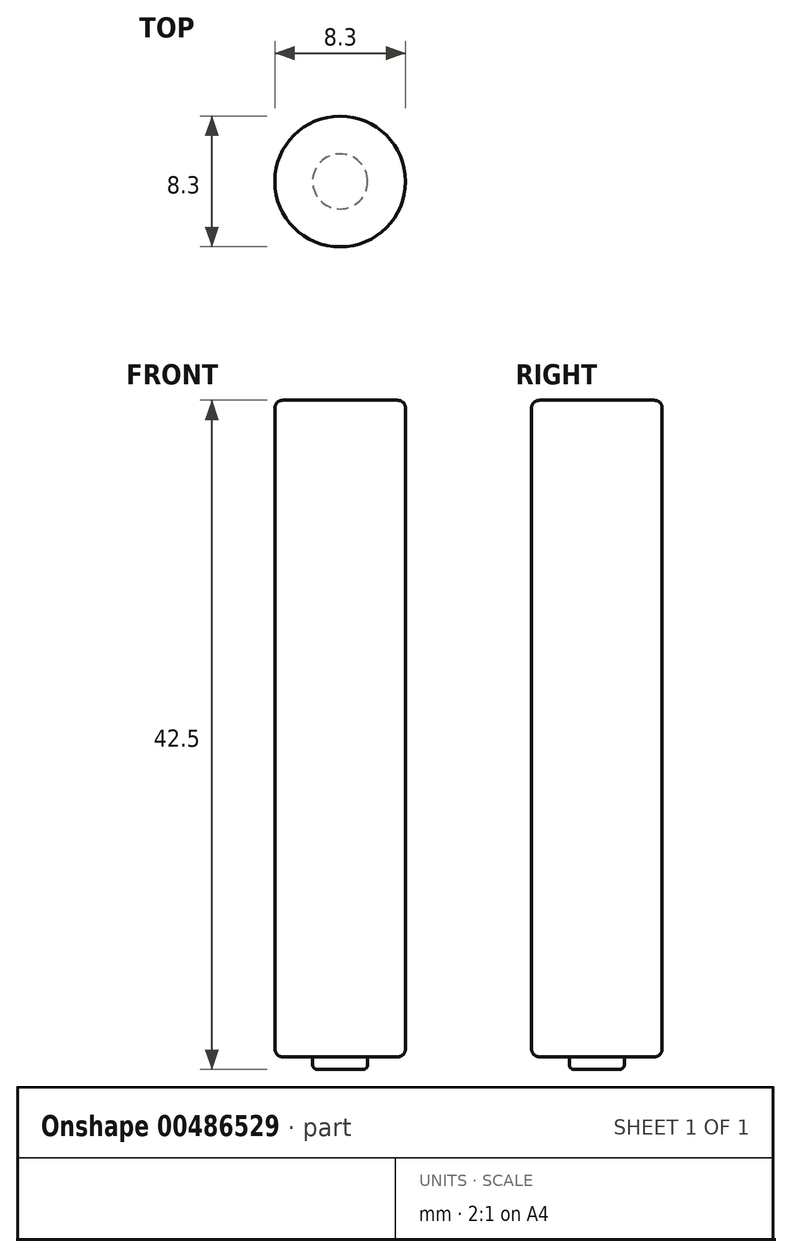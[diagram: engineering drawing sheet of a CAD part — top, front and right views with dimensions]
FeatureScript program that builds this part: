
annotation { "Feature Type Name" : "Feature", "Feature Type Description" : "" }
export const myFeature = defineFeature(function(context is Context, id is Id, definition is map)
    precondition{}
    {
        {
            var Q0;
            Q0=qCreatedBy(makeId("Top.planeOp"),FACE);
            var sketch = newSketch(context, id + "F0", { "sketchPlane" : qUnion([Q0])});
            skCircle(sketch, "E0", {"center": v(0, 0) * mm, "radius": 4.15 * mm});
            skSolve(sketch);
        }
        {
            var Q0;
            Q0=makeQuery(id+"F0.imprint","IMPRINT",FACE,{"disambiguationData":[TD([[makeQuery(id+"F0.imprint","IMPRINT",EDGE,{"derivedFrom":sQuery(id+"F0.wireOp",EDGE,"E0")}),1.0]])]});
            extrude(context, id + "F1", {"entities" : qUnion([Q0]), "depth" : 41.7 * mm});
        }
        {
            var Q0;
            Q0=makeQuery(id+"F1.opExtrude","CAP_FACE",FACE,{"disambiguationData":[OSD([sQuery(id+"F0.wireOp",EDGE,"E0")])],"isStart":true});
            var sketch = newSketch(context, id + "F2", { "sketchPlane" : qUnion([Q0])});
            skCircle(sketch, "E1", {"center": v(0, 0) * mm, "radius": 1.75 * mm});
            skSolve(sketch);
        }
        {
            var Q0;
            Q0=makeQuery(id+"F2.imprint","IMPRINT",FACE,{"disambiguationData":[TD([[makeQuery(id+"F2.imprint","IMPRINT",EDGE,{"derivedFrom":sQuery(id+"F2.wireOp",EDGE,"E1")}),1.0]])]});
            extrude(context, id + "F3", {"entities" : qUnion([Q0]), "operationType" : NewBodyOperationType.ADD, "depth" : 0.8 * mm});
        }
        {
            var Q0;
            Q0=makeQuery(id+"F1.opExtrude","CAP_EDGE",EDGE,{"disambiguationData":[OSD([sQuery(id+"F0.wireOp",EDGE,"E0")])],"isStart":true});
            fillet(context, id + "F4", {"entities" : qUnion([Q0]), "radius" : 0.5 * mm, "tangentPropagation" : true, "allowEdgeOverflow" : false});
        }
        {
            var Q0;
            Q0=makeQuery(id+"F1.opExtrude","CAP_EDGE",EDGE,{"disambiguationData":[OSD([sQuery(id+"F0.wireOp",EDGE,"E0")])],"isStart":false});
            fillet(context, id + "F5", {"entities" : qUnion([Q0]), "radius" : 0.5 * mm, "tangentPropagation" : true, "allowEdgeOverflow" : false});
        }
        {
            var Q0;
            Q0=makeQuery(id+"F3.opExtrude","CAP_EDGE",EDGE,{"disambiguationData":[OSD([sQuery(id+"F2.wireOp",EDGE,"E1")])],"isStart":false});
            var Q1;
            Q1=makeQuery(id+"F3.opExtrude","CAP_EDGE",EDGE,{"disambiguationData":[OSD([sQuery(id+"F2.wireOp",EDGE,"E1")])],"isStart":true});
            fillet(context, id + "F6", {"entities" : qUnion([Q0, Q1]), "radius" : 0.3 * mm, "tangentPropagation" : true, "allowEdgeOverflow" : false});
        }
    });
